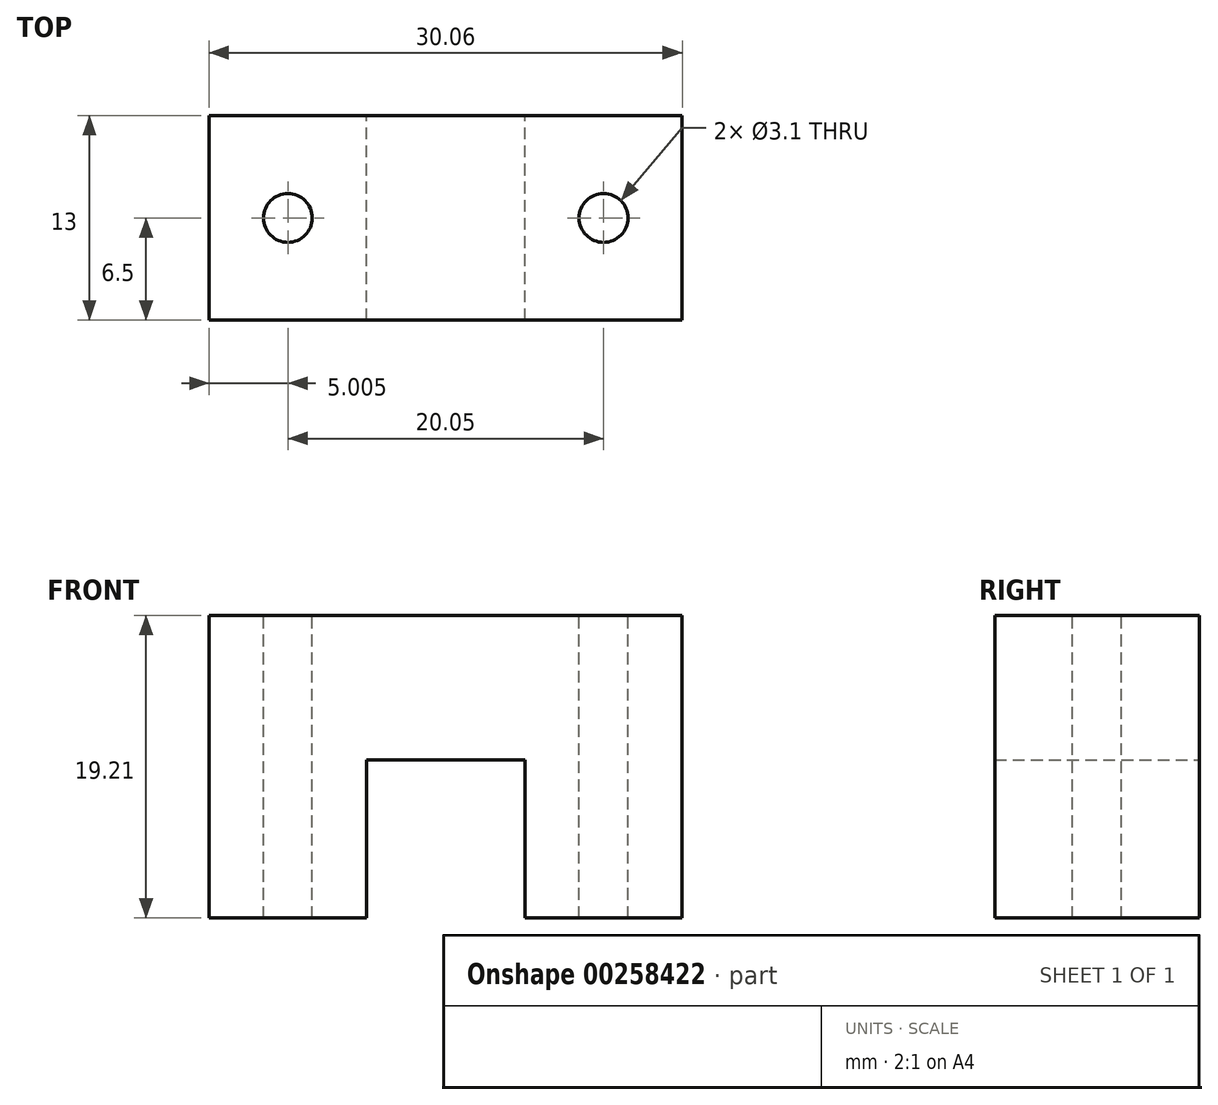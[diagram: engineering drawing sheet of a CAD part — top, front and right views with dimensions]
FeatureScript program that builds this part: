
annotation { "Feature Type Name" : "Feature", "Feature Type Description" : "" }
export const myFeature = defineFeature(function(context is Context, id is Id, definition is map)
    precondition{}
    {
        {
            var Q0;
            Q0=qCreatedBy(makeId("Front.planeOp"),FACE);
            var sketch = newSketch(context, id + "F0", { "sketchPlane" : qUnion([Q0])});
            skLineSegment(sketch, "E0.bottom", {"start": v(5.03, -4.58) * mm, "end": v(-5.03, -4.58) * mm});
            skLineSegment(sketch, "E0.top", {"start": v(15.03, 4.58) * mm, "end": v(-15.03, 4.58) * mm});
            skLineSegment(sketch, "E0.left", {"start": v(15.03, -4.58) * mm, "end": v(15.03, 4.58) * mm});
            skLineSegment(sketch, "E0.right", {"start": v(-15.03, -4.58) * mm, "end": v(-15.03, 4.58) * mm});
            skPoint(sketch, "E0.middle", {"position": v(0, 0) * mm});
            skLineSegment(sketch, "E1.bottom", {"start": v(-15.03, 4.58) * mm, "end": v(-5.03, 4.58) * mm});
            skLineSegment(sketch, "E1.top", {"start": v(-15.03, -14.63) * mm, "end": v(-5.03, -14.63) * mm});
            skLineSegment(sketch, "E1.left", {"start": v(-15.03, 4.58) * mm, "end": v(-15.03, -14.63) * mm});
            skLineSegment(sketch, "E1.right", {"start": v(-5.03, -4.58) * mm, "end": v(-5.03, -14.63) * mm});
            skLineSegment(sketch, "E2.MirrorCS", {"start": v(5.03, -4.58) * mm, "end": v(5.03, -14.63) * mm});
            skLineSegment(sketch, "E3.MirrorCS", {"start": v(15.03, 4.58) * mm, "end": v(5.03, 4.58) * mm});
            skLineSegment(sketch, "E4.MirrorCS", {"start": v(15.03, 4.58) * mm, "end": v(15.03, -14.63) * mm});
            skLineSegment(sketch, "E5.MirrorCS", {"start": v(15.03, -14.63) * mm, "end": v(5.03, -14.63) * mm});
            skPoint(sketch, "E6.orphan", {"position": v(5.03, 4.58) * mm});
            skSolve(sketch);
        }
        {
            var Q0;
            Q0 = qSketchRegion(id + "F0", true);
            extrude(context, id + "F1", {"entities" : qUnion([Q0]), "depth" : 13 * mm});
        }
        {
            var Q0;
            Q0=makeQuery(id+"F1.opExtrude","SWEPT_FACE",FACE,{"disambiguationData":[OSD([sQuery(id+"F0.wireOp",EDGE,"E0.top"),sQuery(id+"F0.wireOp",EDGE,"E1.bottom"),sQuery(id+"F0.wireOp",EDGE,"E3.MirrorCS")])]});
            var sketch = newSketch(context, id + "F2", { "sketchPlane" : qUnion([Q0])});
            skLineSegment(sketch, "E7", {"start": v(0, 13.86) * mm, "end": v(0, -28.94) * mm, "construction": true});
            skLineSegment(sketch, "E8", {"start": v(-15.03, -6.5) * mm, "end": v(15.03, -6.5) * mm, "construction": true});
            skLineSegment(sketch, "E9", {"start": v(15.03, 0) * mm, "end": v(5.03, 0) * mm, "construction": true});
            skLineSegment(sketch, "E10.MirrorCS", {"start": v(-15.03, 0) * mm, "end": v(-5.03, 0) * mm, "construction": true});
            skLineSegment(sketch, "E11", {"start": v(-5.03, 0) * mm, "end": v(5.03, 0) * mm, "construction": true});
            skLineSegment(sketch, "E12", {"start": v(10.03, 0) * mm, "end": v(10.03, -13) * mm, "construction": true});
            skLineSegment(sketch, "E13", {"start": v(-10.03, 0) * mm, "end": v(-10.03, -13) * mm, "construction": true});
            skCircle(sketch, "E14", {"center": v(-10.03, -6.5) * mm, "radius": 1.55 * mm});
            skCircle(sketch, "E15", {"center": v(10.03, -6.5) * mm, "radius": 1.55 * mm});
            skSolve(sketch);
        }
        {
            var Q0;
            Q0=makeQuery(id+"F2.imprint","IMPRINT",FACE,{"disambiguationData":[TD([[makeQuery(id+"F2.imprint","IMPRINT",EDGE,{"derivedFrom":sQuery(id+"F2.wireOp",EDGE,"E14")}),1.0]])]});
            var Q1;
            Q1=makeQuery(id+"F2.imprint","IMPRINT",FACE,{"disambiguationData":[TD([[makeQuery(id+"F2.imprint","IMPRINT",EDGE,{"derivedFrom":sQuery(id+"F2.wireOp",EDGE,"E15")}),1.0]])]});
            extrude(context, id + "F3", {"entities" : qUnion([Q0, Q1]), "operationType" : NewBodyOperationType.REMOVE, "oppositeDirection" : true, "depth" : 25 * mm});
        }
    });
